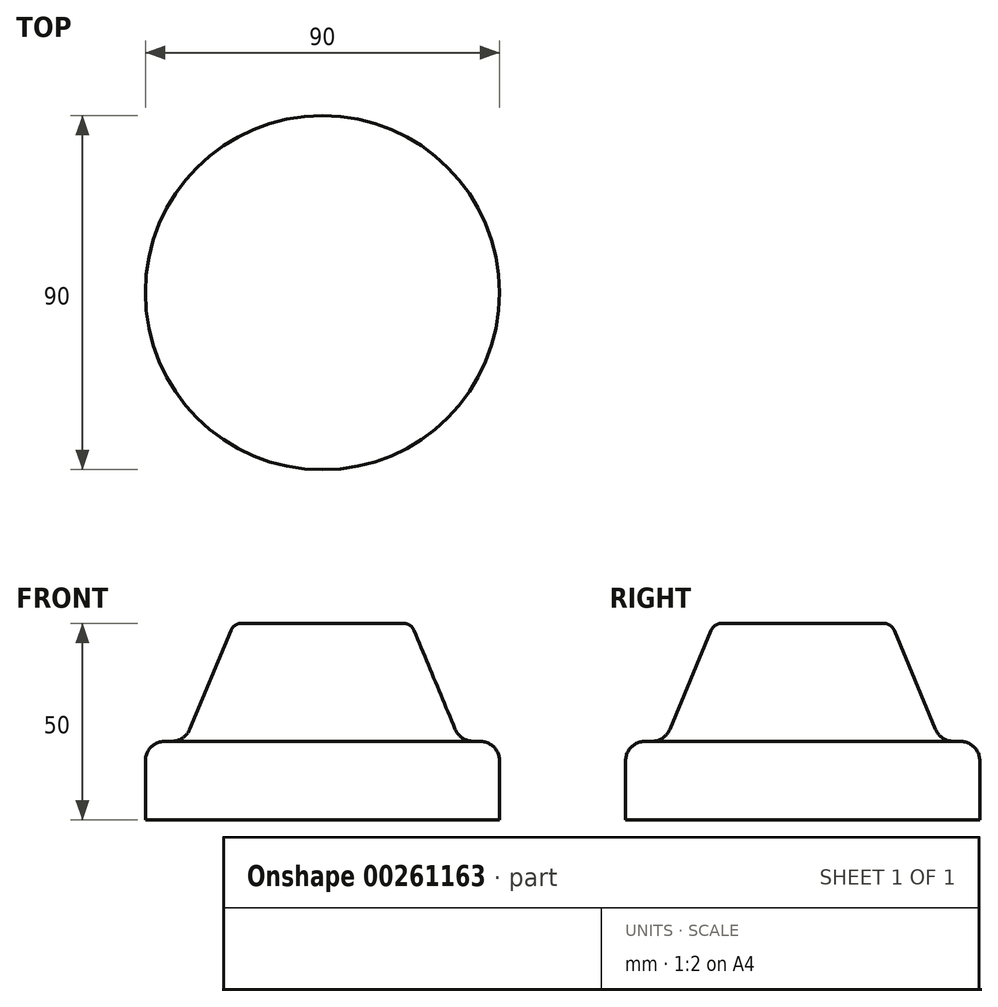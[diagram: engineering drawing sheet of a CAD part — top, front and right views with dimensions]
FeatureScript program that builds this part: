
annotation { "Feature Type Name" : "Feature", "Feature Type Description" : "" }
export const myFeature = defineFeature(function(context is Context, id is Id, definition is map)
    precondition{}
    {
        {
            var Q0;
            Q0=qCreatedBy(makeId("Front.planeOp"),FACE);
            var sketch = newSketch(context, id + "F0", { "sketchPlane" : qUnion([Q0])});
            skLineSegment(sketch, "E0", {"start": v(0, 50) * mm, "end": v(0, 0) * mm});
            skLineSegment(sketch, "E1", {"start": v(0, 0) * mm, "end": v(45, 0) * mm});
            skLineSegment(sketch, "E2", {"start": v(45, 0) * mm, "end": v(45, 15) * mm});
            skLineSegment(sketch, "E3", {"start": v(40, 20) * mm, "end": v(38.33, 20) * mm});
            skLineSegment(sketch, "E4", {"start": v(33.72, 23.08) * mm, "end": v(23.27, 48.15) * mm});
            skLineSegment(sketch, "E5", {"start": v(20.5, 50) * mm, "end": v(0, 50) * mm});
            skPoint(sketch, "E6.visualSharp", {"position": v(22.5, 50) * mm});
            skArc(sketch, "E6.filletArc", {"start": v(23.27, 48.15) * mm, "mid": v(22.16, 49.5) * mm, "end": v(20.5, 50) * mm});
            skPoint(sketch, "E7.visualSharp", {"position": v(35, 20) * mm});
            skArc(sketch, "E7.filletArc", {"start": v(33.72, 23.08) * mm, "mid": v(35.56, 20.84) * mm, "end": v(38.33, 20) * mm});
            skPoint(sketch, "E8.visualSharp", {"position": v(45, 20) * mm});
            skArc(sketch, "E8.filletArc", {"start": v(45, 15) * mm, "mid": v(43.54, 18.54) * mm, "end": v(40, 20) * mm});
            skLineSegment(sketch, "E9", {"start": v(0, 68.92) * mm, "end": v(0, -45.02) * mm});
            skLineSegment(sketch, "E10", {"start": v(0, -45.02) * mm, "end": v(0, 68.92) * mm, "construction": true});
            skSolve(sketch);
        }
        {
            var Q0;
            Q0 = qSketchRegion(id + "F0", true);
            var Q1;
            Q1=sQuery(id+"F0.wireOp",EDGE,"E9");
            revolve(context, id + "F1", {"entities" : qUnion([Q0]), "axis" : qUnion([Q1]), "revolveType" : RevolveType.FULL});
        }
    });
